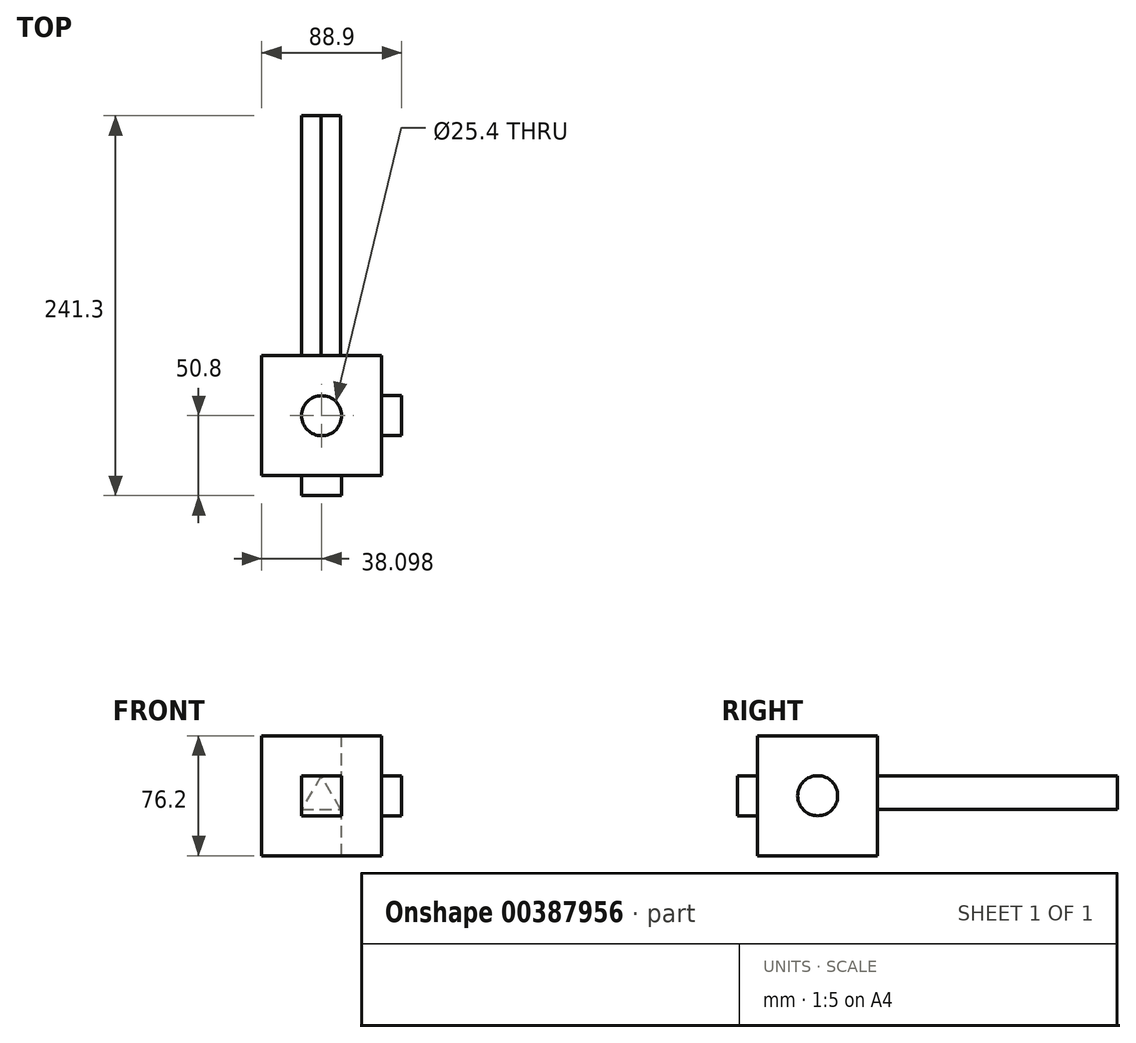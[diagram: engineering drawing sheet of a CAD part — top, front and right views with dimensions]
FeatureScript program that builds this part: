
annotation { "Feature Type Name" : "Feature", "Feature Type Description" : "" }
export const myFeature = defineFeature(function(context is Context, id is Id, definition is map)
    precondition{}
    {
        {
            var Q0;
            Q0=qCreatedBy(makeId("Front.planeOp"),FACE);
            var sketch = newSketch(context, id + "F0", { "sketchPlane" : qUnion([Q0])});
            skLineSegment(sketch, "E0.bottom", {"start": v(-47.94, 35.56) * mm, "end": v(28.26, 35.56) * mm});
            skLineSegment(sketch, "E0.top", {"start": v(-47.94, -40.64) * mm, "end": v(28.26, -40.64) * mm});
            skLineSegment(sketch, "E0.left", {"start": v(-47.94, 35.56) * mm, "end": v(-47.94, -40.64) * mm});
            skLineSegment(sketch, "E0.right", {"start": v(28.26, 35.56) * mm, "end": v(28.26, -40.64) * mm});
            skSolve(sketch);
        }
        {
            var Q0;
            Q0 = qSketchRegion(id + "F0", true);
            extrude(context, id + "F1", {"entities" : qUnion([Q0]), "depth" : 76.2 * mm});
        }
        {
            var Q0;
            Q0=makeQuery(id+"F1.opExtrude","SWEPT_FACE",FACE,{"disambiguationData":[OSD([sQuery(id+"F0.wireOp",EDGE,"E0.bottom")])]});
            var sketch = newSketch(context, id + "F2", { "sketchPlane" : qUnion([Q0])});
            skPoint(sketch, "E1", {"position": v(-9.84, -38.1) * mm});
            skSolve(sketch);
        }
        {
            var Q0;
            Q0=sQuery(id+"F2.wireOp",VERTEX,"E1");
            var Q1;
            Q1=makeQuery(id+"F1.opExtrude","SWEPT_BODY",BODY,{"disambiguationData":[OSD([sQuery(id+"F0.wireOp",EDGE,"E0.bottom"),sQuery(id+"F0.wireOp",EDGE,"E0.top"),sQuery(id+"F0.wireOp",EDGE,"E0.left"),sQuery(id+"F0.wireOp",EDGE,"E0.right")])]});
            hole(context, id + "F3", {"style" : HoleStyle.SIMPLE, "endStyle" : HoleEndStyle.THROUGH, "holeDiameter" : 25.4 * mm, "isTappedThrough" : true, "tappedDepth" : 12.7 * mm, "tapClearance" : 3, "locations" : qUnion([Q0]), "scope" : qUnion([Q1])});
        }
        {
            var Q0;
            Q0=makeQuery(id+"F1.opExtrude","CAP_FACE",FACE,{"disambiguationData":[OSD([sQuery(id+"F0.wireOp",EDGE,"E0.bottom"),sQuery(id+"F0.wireOp",EDGE,"E0.top"),sQuery(id+"F0.wireOp",EDGE,"E0.left"),sQuery(id+"F0.wireOp",EDGE,"E0.right")])],"isStart":false});
            var sketch = newSketch(context, id + "F4", { "sketchPlane" : qUnion([Q0])});
            skLineSegment(sketch, "E2.bottom", {"start": v(-22.54, 10.16) * mm, "end": v(2.86, 10.16) * mm});
            skLineSegment(sketch, "E2.top", {"start": v(-22.54, -15.24) * mm, "end": v(2.86, -15.24) * mm});
            skLineSegment(sketch, "E2.left", {"start": v(-22.54, 10.16) * mm, "end": v(-22.54, -15.24) * mm});
            skLineSegment(sketch, "E2.right", {"start": v(2.86, 10.16) * mm, "end": v(2.86, -15.24) * mm});
            skSolve(sketch);
        }
        {
            var Q0;
            Q0 = qSketchRegion(id + "F4", true);
            extrude(context, id + "F5", {"entities" : qUnion([Q0]), "operationType" : NewBodyOperationType.ADD, "depth" : 12.7 * mm});
        }
        {
            var Q0;
            Q0=makeQuery(id+"F1.opExtrude","SWEPT_FACE",FACE,{"disambiguationData":[OSD([sQuery(id+"F0.wireOp",EDGE,"E0.right")])]});
            var sketch = newSketch(context, id + "F6", { "sketchPlane" : qUnion([Q0])});
            skCircle(sketch, "E3", {"center": v(-38.1, -2.54) * mm, "radius": 12.7 * mm});
            skSolve(sketch);
        }
        {
            var Q0;
            Q0 = qSketchRegion(id + "F6", true);
            extrude(context, id + "F7", {"entities" : qUnion([Q0]), "operationType" : NewBodyOperationType.ADD, "depth" : 12.7 * mm});
        }
        {
            var Q0;
            Q0=makeQuery(id+"F1.opExtrude","CAP_FACE",FACE,{"disambiguationData":[OSD([sQuery(id+"F0.wireOp",EDGE,"E0.bottom"),sQuery(id+"F0.wireOp",EDGE,"E0.top"),sQuery(id+"F0.wireOp",EDGE,"E0.left"),sQuery(id+"F0.wireOp",EDGE,"E0.right")])],"isStart":true});
            var sketch = newSketch(context, id + "F8", { "sketchPlane" : qUnion([Q0])});
            skCircle(sketch, "E4.cCircle", {"center": v(10.15, -4.15) * mm, "radius": 7.15 * mm, "construction": true});
            skLineSegment(sketch, "E4.0", {"start": v(22.54, -11.3) * mm, "end": v(-2.23, -11.3) * mm});
            skLineSegment(sketch, "E4.1", {"start": v(-2.23, -11.3) * mm, "end": v(10.15, 10.16) * mm});
            skLineSegment(sketch, "E4.2", {"start": v(10.15, 10.16) * mm, "end": v(22.54, -11.3) * mm});
            skPoint(sketch, "E4.0.midPoint", {"position": v(10.15, -11.3) * mm});
            skSolve(sketch);
        }
        {
            var Q0;
            Q0 = qSketchRegion(id + "F8", true);
            extrude(context, id + "F9", {"entities" : qUnion([Q0]), "operationType" : NewBodyOperationType.ADD, "depth" : 152.4 * mm});
        }
    });
